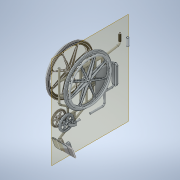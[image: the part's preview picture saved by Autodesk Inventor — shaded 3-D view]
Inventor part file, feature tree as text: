
AUTODESK INVENTOR PART (.ipt)
format: ipt  version: 2021 (Build 250183000, 183)  size: 1,123,328 bytes
history: native  units: mm
features: other x13, plane x1, extrude x1, mirror x1, sketch x1
ambient origin geometry x8: Origin, YZ Plane, XZ Plane, XY Plane, X Axis, Y Axis, Z Axis, Center Point
bodies: Solid1 (feature_tree), Solid2 (feature_tree), Solid5 (feature_tree), Solid7 (feature_tree), Solid10 (feature_tree), Solid11 (feature_tree), Solid13 (feature_tree), Solid17 (feature_tree), Solid18 (feature_tree), Solid19 (feature_tree), Solid20 (feature_tree), Solid24 (feature_tree), Solid26 (feature_tree)
feature tree (17):
  plane  "Work Plane1"
  extrude  "Extrusion1"  Depth=500.0mm TaperAngle=0.0deg
  mirror  "Mirror1"
  sketch  "Sketch1"  dims[d0=50.0mm d1=500.0mm d2=0.0mm]
  other  "SideFrame_1:1"
  other  "SideFrame_1:2"
  other  "SideFrame_1:5"
  other  "SideFrame_1:7"
  other  "Arm_3:1"
  other  "Arm_3:2"
  other  "ArmPad_5:1"
  other  "WheelLarge_8:1"
  other  "WheelLarge_8:2"
  other  "WheelSmall_16:1"
  other  "CasterFork_17:1"
  other  "FootRest_12:1"
  other  "Grip_14:1"
